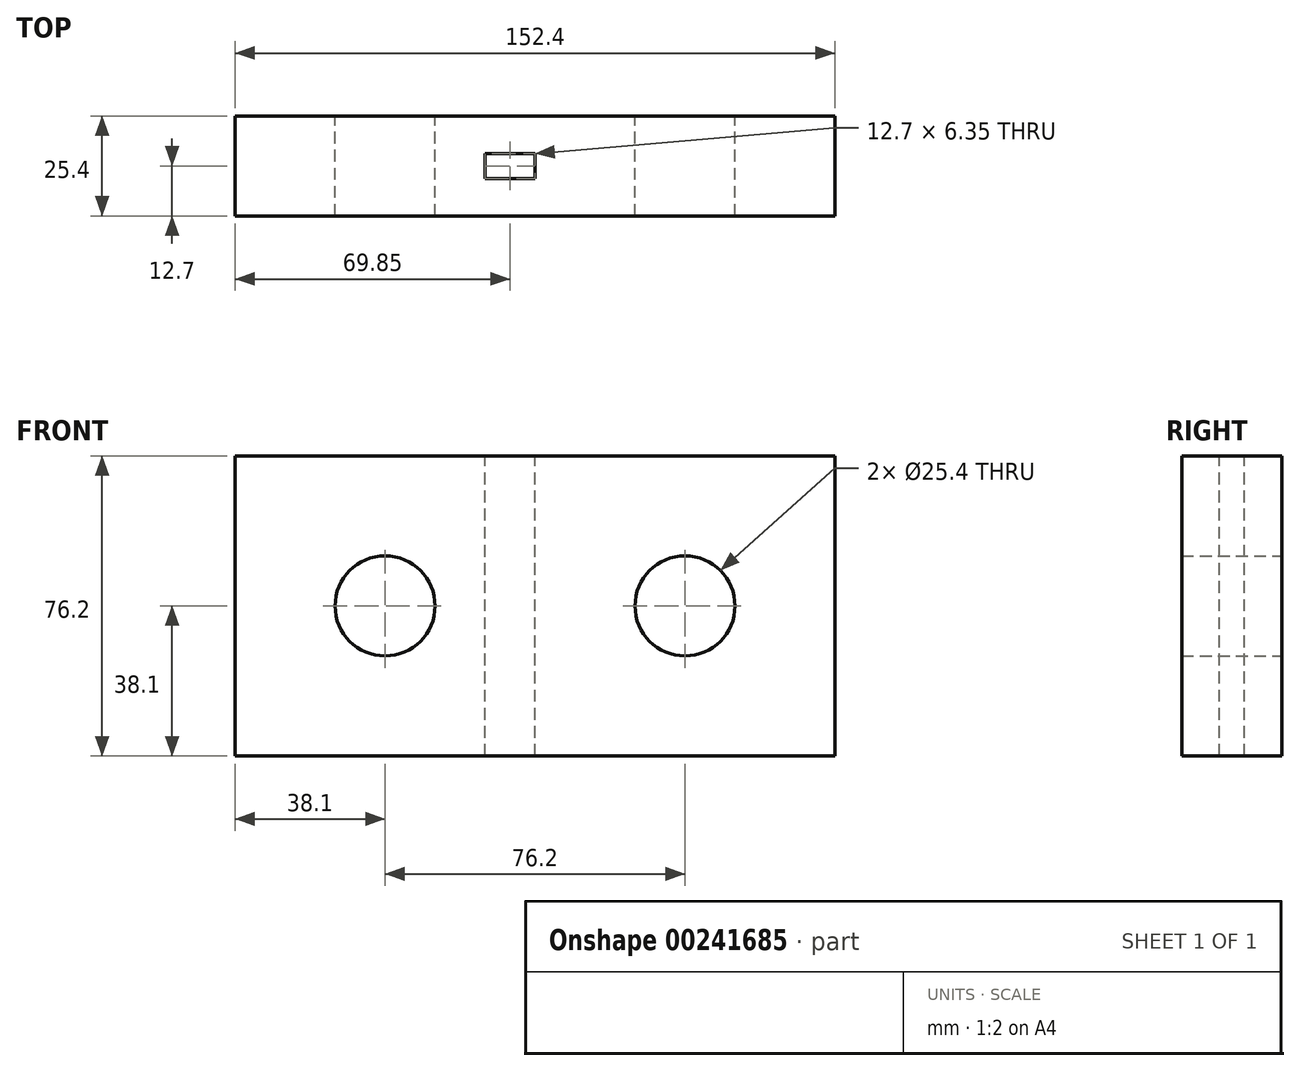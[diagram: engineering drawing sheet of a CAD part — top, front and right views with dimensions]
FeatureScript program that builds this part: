
annotation { "Feature Type Name" : "Feature", "Feature Type Description" : "" }
export const myFeature = defineFeature(function(context is Context, id is Id, definition is map)
    precondition{}
    {
        {
            var Q0;
            Q0=qCreatedBy(makeId("Front.planeOp"),FACE);
            var sketch = newSketch(context, id + "F0", { "sketchPlane" : qUnion([Q0])});
            skLineSegment(sketch, "E0.bottom", {"start": v(76.2, -38.1) * mm, "end": v(-76.2, -38.1) * mm});
            skLineSegment(sketch, "E0.top", {"start": v(76.2, 38.1) * mm, "end": v(-76.2, 38.1) * mm});
            skLineSegment(sketch, "E0.left", {"start": v(76.2, -38.1) * mm, "end": v(76.2, 38.1) * mm});
            skLineSegment(sketch, "E0.right", {"start": v(-76.2, -38.1) * mm, "end": v(-76.2, 38.1) * mm});
            skPoint(sketch, "E0.middle", {"position": v(0, 0) * mm});
            skCircle(sketch, "E1", {"center": v(38.1, 0) * mm, "radius": 12.7 * mm});
            skCircle(sketch, "E2", {"center": v(-38.1, 0) * mm, "radius": 12.7 * mm});
            skSolve(sketch);
        }
        {
            var Q0;
            Q0=qCreatedBy(makeId("Top.planeOp"),FACE);
            var sketch = newSketch(context, id + "F1", { "sketchPlane" : qUnion([Q0])});
            skLineSegment(sketch, "E3.bottom", {"start": v(0, -9.52) * mm, "end": v(-12.7, -9.52) * mm});
            skLineSegment(sketch, "E3.top", {"start": v(0, -15.88) * mm, "end": v(-12.7, -15.88) * mm});
            skLineSegment(sketch, "E3.left", {"start": v(0, -9.52) * mm, "end": v(0, -15.88) * mm});
            skLineSegment(sketch, "E3.right", {"start": v(-12.7, -9.53) * mm, "end": v(-12.7, -15.88) * mm});
            skSolve(sketch);
        }
        {
            var Q0;
            Q0 = qSketchRegion(id + "F0", true);
            extrude(context, id + "F2", {"entities" : qUnion([Q0]), "depth" : 25.4 * mm});
        }
        {
            var Q0;
            Q0 = qSketchRegion(id + "F1", true);
            extrude(context, id + "F3", {"entities" : qUnion([Q0]), "operationType" : NewBodyOperationType.REMOVE, "oppositeDirection" : true, "depth" : 62.23 * mm});
        }
        {
            var Q0;
            Q0 = qSketchRegion(id + "F1", true);
            extrude(context, id + "F4", {"entities" : qUnion([Q0]), "operationType" : NewBodyOperationType.REMOVE, "depth" : 55.37 * mm});
        }
    });
